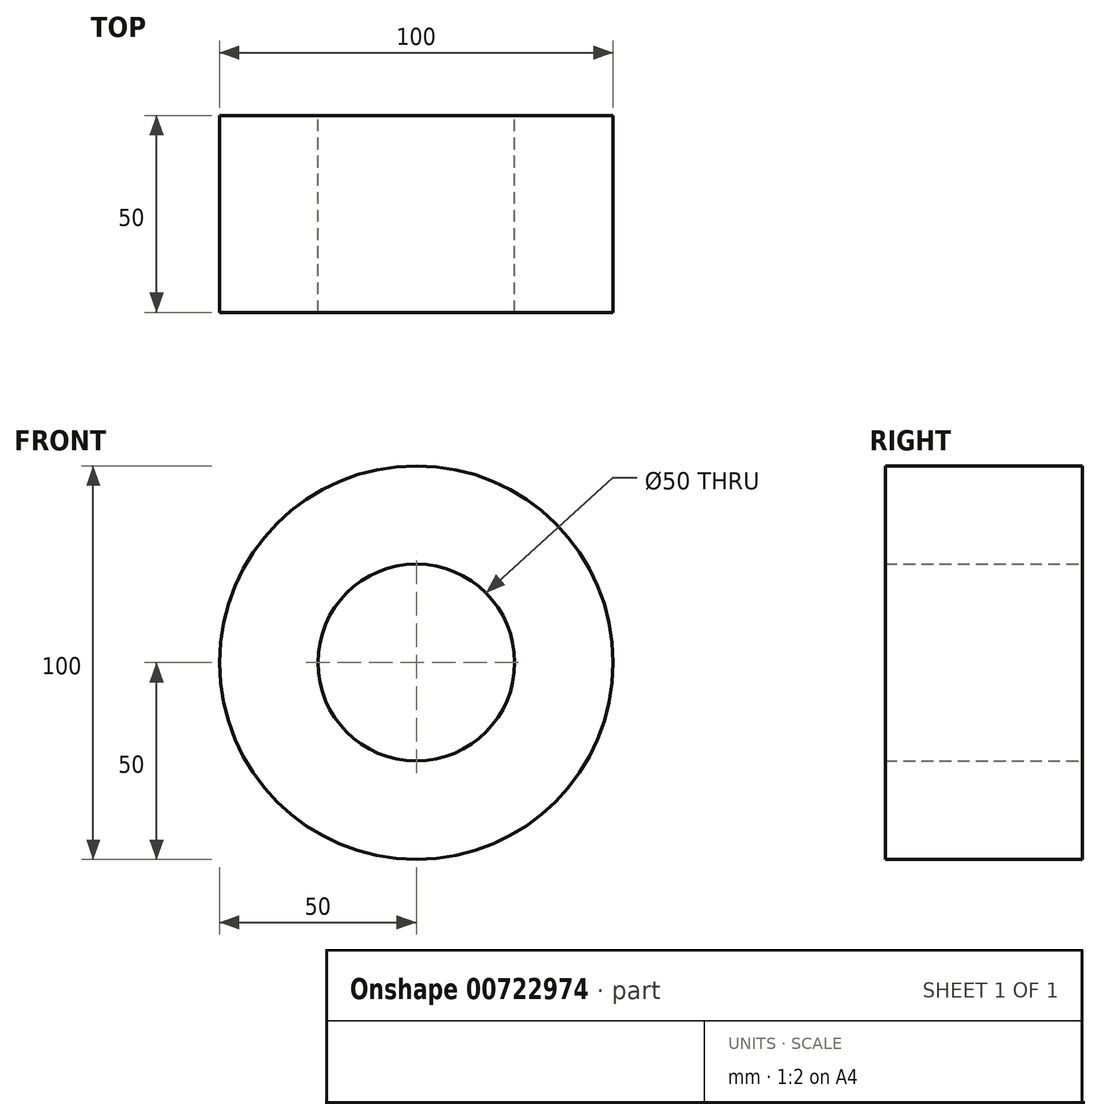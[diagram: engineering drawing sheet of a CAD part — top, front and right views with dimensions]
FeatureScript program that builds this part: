
annotation { "Feature Type Name" : "Feature", "Feature Type Description" : "" }
export const myFeature = defineFeature(function(context is Context, id is Id, definition is map)
    precondition{}
    {
        {
            var Q0;
            Q0=qCreatedBy(makeId("Front.planeOp"),FACE);
            var sketch = newSketch(context, id + "F0", { "sketchPlane" : qUnion([Q0])});
            skCircle(sketch, "E0", {"center": v(0, 0) * mm, "radius": 50 * mm});
            skCircle(sketch, "E1", {"center": v(0, 0) * mm, "radius": 25 * mm});
            skSolve(sketch);
        }
        {
            var Q0;
            Q0=makeQuery(id+"F0.imprint","IMPRINT",FACE,{"disambiguationData":[TD([[makeQuery(id+"F0.imprint","IMPRINT",EDGE,{"derivedFrom":sQuery(id+"F0.wireOp",EDGE,"E0")}),1.0]])]});
            var Q1;
            Q1=sQuery(id+"F0.wireOp",EDGE,"E0");
            extrude(context, id + "F1", {"entities" : qUnion([Q0]), "surfaceEntities" : qUnion([Q1]), "depth" : 50 * mm, "offsetDistance" : 25 * mm, "symmetric" : true});
        }
    });
